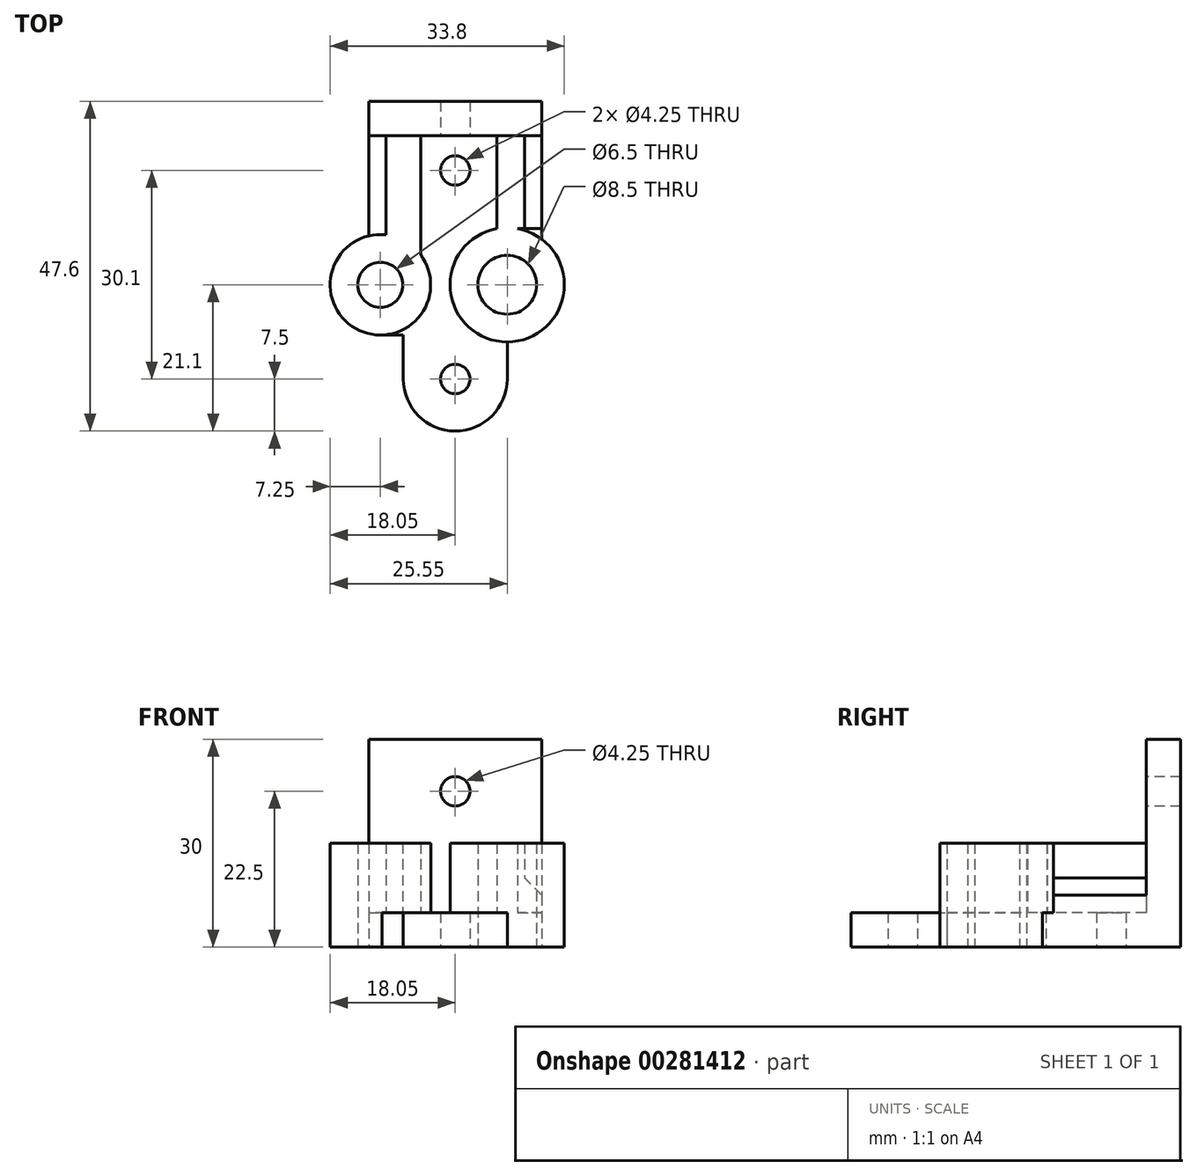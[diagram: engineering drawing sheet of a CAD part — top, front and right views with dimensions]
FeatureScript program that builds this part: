
annotation { "Feature Type Name" : "Feature", "Feature Type Description" : "" }
export const myFeature = defineFeature(function(context is Context, id is Id, definition is map)
    precondition{}
    {
        {
            var Q0;
            Q0=qCreatedBy(makeId("Top.planeOp"),FACE);
            var sketch = newSketch(context, id + "F0", { "sketchPlane" : qUnion([Q0])});
            skLineSegment(sketch, "E0", {"start": v(0, 26.5) * mm, "end": v(12.5, 26.5) * mm});
            skLineSegment(sketch, "E1", {"start": v(12.5, 26.5) * mm, "end": v(12.5, 6.56) * mm});
            skLineSegment(sketch, "E2", {"start": v(0, -21.1) * mm, "end": v(0, -21.1) * mm});
            skCircle(sketch, "E3", {"center": v(0, 16.5) * mm, "radius": 2.12 * mm});
            skCircle(sketch, "E4", {"center": v(0, -13.6) * mm, "radius": 2.12 * mm});
            skCircle(sketch, "E5", {"center": v(-10.8, 0) * mm, "radius": 3.25 * mm});
            skCircle(sketch, "E6", {"center": v(7.5, 0) * mm, "radius": 4.25 * mm});
            skLineSegment(sketch, "E7.MirrorCS", {"start": v(0, 26.5) * mm, "end": v(-12.5, 26.5) * mm});
            skLineSegment(sketch, "E8.MirrorCS", {"start": v(-12.5, 26.5) * mm, "end": v(-12.5, 7.05) * mm});
            skLineSegment(sketch, "E9", {"start": v(7.5, -13.6) * mm, "end": v(7.5, -8.25) * mm});
            skArc(sketch, "E10", {"start": v(-10.57, -7.25) * mm, "mid": v(-17.98, -0.97) * mm, "end": v(-12.5, 7.05) * mm});
            skArc(sketch, "E11", {"start": v(12.5, 6.56) * mm, "mid": v(15.32, -2.64) * mm, "end": v(7.5, -8.25) * mm});
            skPoint(sketch, "E12.trimOffspring.end.orphan", {"position": v(-12.5, -21.1) * mm});
            skPoint(sketch, "E13.orphan", {"position": v(12.5, -21.1) * mm});
            skPoint(sketch, "E14.visualSharp", {"position": v(-7.5, -21.1) * mm});
            skArc(sketch, "E14.filletArc", {"start": v(-7.5, -13.6) * mm, "mid": v(-5.3, -18.9) * mm, "end": v(0, -21.1) * mm});
            skPoint(sketch, "E15.visualSharp", {"position": v(7.5, -21.1) * mm});
            skArc(sketch, "E15.filletArc", {"start": v(0, -21.1) * mm, "mid": v(5.3, -18.9) * mm, "end": v(7.5, -13.6) * mm});
            skLineSegment(sketch, "E16", {"start": v(-10.57, -7.25) * mm, "end": v(-7.5, -7.25) * mm});
            skLineSegment(sketch, "E17", {"start": v(-7.5, -13.6) * mm, "end": v(-7.5, -7.25) * mm});
            skSolve(sketch);
        }
        {
            var Q0;
            Q0=qSketchRegion(id+"F0",true);
            extrude(context, id + "F1", {"entities" : qUnion([Q0]), "depth" : 5 * mm});
        }
        {
            var Q0;
            Q0=makeQuery(id+"F1.opExtrude","CAP_FACE",FACE,{"disambiguationData":[OSD([sQuery(id+"F0.wireOp",EDGE,"E0"),sQuery(id+"F0.wireOp",EDGE,"E1"),sQuery(id+"F0.wireOp",EDGE,"E2"),sQuery(id+"F0.wireOp",EDGE,"E3"),sQuery(id+"F0.wireOp",EDGE,"E4"),sQuery(id+"F0.wireOp",EDGE,"E5"),sQuery(id+"F0.wireOp",EDGE,"E6"),sQuery(id+"F0.wireOp",EDGE,"E7.MirrorCS"),sQuery(id+"F0.wireOp",EDGE,"E8.MirrorCS"),sQuery(id+"F0.wireOp",EDGE,"E2"),sQuery(id+"F0.wireOp",EDGE,"E9"),sQuery(id+"F0.wireOp",EDGE,"0SpK3guX-SHqh-8jfR-4gbB-wGZ5s9GyuE9B"),sQuery(id+"F0.wireOp",EDGE,"kbQLnVgn-lxyG-YleV-xpZB-5WNRk4PG5Xhd"),sQuery(id+"F0.wireOp",EDGE,"E10"),sQuery(id+"F0.wireOp",EDGE,"E11")])],"isStart":false});
            var sketch = newSketch(context, id + "F2", { "sketchPlane" : qUnion([Q0])});
            skLineSegment(sketch, "E18.bottom", {"start": v(-12.5, 26.5) * mm, "end": v(12.5, 26.5) * mm});
            skLineSegment(sketch, "E18.top", {"start": v(-12.5, 21.5) * mm, "end": v(12.5, 21.5) * mm});
            skLineSegment(sketch, "E18.left", {"start": v(-12.5, 26.5) * mm, "end": v(-12.5, 21.5) * mm});
            skLineSegment(sketch, "E18.right", {"start": v(12.5, 26.5) * mm, "end": v(12.5, 21.5) * mm});
            skSolve(sketch);
        }
        {
            var Q0;
            Q0=qSketchRegion(id+"F2",true);
            extrude(context, id + "F3", {"entities" : qUnion([Q0]), "operationType" : NewBodyOperationType.ADD, "depth" : 25 * mm});
        }
        {
            var Q0;
            Q0=makeQuery(id+"F1.opExtrude","CAP_FACE",FACE,{"disambiguationData":[OSD([sQuery(id+"F0.wireOp",EDGE,"E0"),sQuery(id+"F0.wireOp",EDGE,"E1"),sQuery(id+"F0.wireOp",EDGE,"E3"),sQuery(id+"F0.wireOp",EDGE,"E4"),sQuery(id+"F0.wireOp",EDGE,"E5"),sQuery(id+"F0.wireOp",EDGE,"E6"),sQuery(id+"F0.wireOp",EDGE,"E7.MirrorCS"),sQuery(id+"F0.wireOp",EDGE,"E8.MirrorCS"),sQuery(id+"F0.wireOp",EDGE,"E9"),sQuery(id+"F0.wireOp",EDGE,"0SpK3guX-SHqh-8jfR-4gbB-wGZ5s9GyuE9B"),sQuery(id+"F0.wireOp",EDGE,"kbQLnVgn-lxyG-YleV-xpZB-5WNRk4PG5Xhd"),sQuery(id+"F0.wireOp",EDGE,"E10"),sQuery(id+"F0.wireOp",EDGE,"E11"),sQuery(id+"F0.wireOp",EDGE,"E14.filletArc"),sQuery(id+"F0.wireOp",EDGE,"E15.filletArc")])],"isStart":false});
            var sketch = newSketch(context, id + "F4", { "sketchPlane" : qUnion([Q0])});
            skCircle(sketch, "E19", {"center": v(-10.8, 0) * mm, "radius": 3.25 * mm});
            skCircle(sketch, "E20", {"center": v(-10.8, 0) * mm, "radius": 7.25 * mm});
            skCircle(sketch, "E21", {"center": v(7.5, 0) * mm, "radius": 4.25 * mm});
            skCircle(sketch, "E22", {"center": v(7.5, 0) * mm, "radius": 8.25 * mm});
            skSolve(sketch);
        }
        {
            var Q0;
            Q0=qSketchRegion(id+"F4",true);
            extrude(context, id + "F5", {"entities" : qUnion([Q0]), "operationType" : NewBodyOperationType.ADD, "depth" : 10 * mm});
        }
        {
            var Q0;
            Q0=makeQuery(id+"F3.opExtrude","SWEPT_FACE",FACE,{"disambiguationData":[OSD([sQuery(id+"F2.wireOp",EDGE,"E18.top")])]});
            var sketch = newSketch(context, id + "F6", { "sketchPlane" : qUnion([Q0])});
            skCircle(sketch, "E23", {"center": v(0, 22.5) * mm, "radius": 2.12 * mm});
            skSolve(sketch);
        }
        {
            var Q0;
            Q0=qSketchRegion(id+"F6",true);
            extrude(context, id + "F7", {"entities" : qUnion([Q0]), "operationType" : NewBodyOperationType.REMOVE, "endBound" : BoundingType.THROUGH_ALL, "oppositeDirection" : true, "depth" : 25 * mm});
        }
        {
            var Q0;
            Q0=makeQuery(id+"F1.opExtrude","CAP_FACE",FACE,{"disambiguationData":[OSD([sQuery(id+"F0.wireOp",EDGE,"E0"),sQuery(id+"F0.wireOp",EDGE,"E1"),sQuery(id+"F0.wireOp",EDGE,"E3"),sQuery(id+"F0.wireOp",EDGE,"E4"),sQuery(id+"F0.wireOp",EDGE,"E5"),sQuery(id+"F0.wireOp",EDGE,"E6"),sQuery(id+"F0.wireOp",EDGE,"E7.MirrorCS"),sQuery(id+"F0.wireOp",EDGE,"E8.MirrorCS"),sQuery(id+"F0.wireOp",EDGE,"E9"),sQuery(id+"F0.wireOp",EDGE,"0SpK3guX-SHqh-8jfR-4gbB-wGZ5s9GyuE9B"),sQuery(id+"F0.wireOp",EDGE,"kbQLnVgn-lxyG-YleV-xpZB-5WNRk4PG5Xhd"),sQuery(id+"F0.wireOp",EDGE,"E10"),sQuery(id+"F0.wireOp",EDGE,"E11"),sQuery(id+"F0.wireOp",EDGE,"E14.filletArc"),sQuery(id+"F0.wireOp",EDGE,"E15.filletArc")])],"isStart":false});
            var sketch = newSketch(context, id + "F8", { "sketchPlane" : qUnion([Q0])});
            skLineSegment(sketch, "E24.bottom", {"start": v(-10, 21.5) * mm, "end": v(-5, 21.5) * mm});
            skLineSegment(sketch, "E24.top", {"start": v(-10, 4.35) * mm, "end": v(-5, 4.35) * mm});
            skLineSegment(sketch, "E24.left", {"start": v(-10, 21.5) * mm, "end": v(-10, 4.35) * mm});
            skLineSegment(sketch, "E24.right", {"start": v(-5, 21.5) * mm, "end": v(-5, 4.35) * mm});
            skLineSegment(sketch, "E25.bottom", {"start": v(6, 21.5) * mm, "end": v(10, 21.5) * mm});
            skLineSegment(sketch, "E25.top", {"start": v(6, 8.11) * mm, "end": v(10, 8.11) * mm});
            skLineSegment(sketch, "E25.left", {"start": v(6, 21.5) * mm, "end": v(6, 8.11) * mm});
            skLineSegment(sketch, "E25.right", {"start": v(10, 21.5) * mm, "end": v(10, 8.11) * mm});
            skSolve(sketch);
        }
        {
            var Q0;
            Q0=qSketchRegion(id+"F8",true);
            extrude(context, id + "F9", {"entities" : qUnion([Q0]), "operationType" : NewBodyOperationType.ADD, "depth" : 10 * mm});
        }
        {
            var Q0;
            Q0=makeQuery(id+"F9.opExtrude","CAP_EDGE",EDGE,{"disambiguationData":[OSD([sQuery(id+"F8.wireOp",EDGE,"E24.bottom")])],"isStart":false});
            var Q1;
            Q1=makeQuery(id+"F9.opExtrude","CAP_EDGE",EDGE,{"disambiguationData":[OSD([sQuery(id+"F8.wireOp",EDGE,"E25.bottom")])],"isStart":false});
            var Q2;
            Q2=makeQuery(id+"F9.opExtrude","CAP_EDGE",EDGE,{"disambiguationData":[OSD([sQuery(id+"F8.wireOp",EDGE,"E24.left")])],"isStart":true});
            var Q3;
            Q3=makeQuery(id+"F9.opExtrude","CAP_EDGE",EDGE,{"disambiguationData":[OSD([sQuery(id+"F8.wireOp",EDGE,"E25.right")])],"isStart":true});
            chamfer(context, id + "F10", {"entities" : qUnion([Q0, Q1, Q2, Q3]), "width" : 5 * mm, "tangentPropagation" : true});
        }
    });
